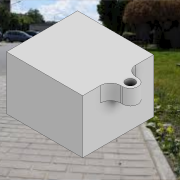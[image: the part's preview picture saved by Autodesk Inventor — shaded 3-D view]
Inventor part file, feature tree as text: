
AUTODESK INVENTOR PART (.ipt)
format: ipt  version: 2021 (Build 250183000, 183)  size: 265,216 bytes
history: native  units: mm
features: sketch x6, extrude x5, projected_geometry x3, hole x1, fillet x1
ambient origin geometry x8: Origin, YZ Plane, XZ Plane, XY Plane, X Axis, Y Axis, Z Axis, Center Point
bodies: Solid2 (feature_tree), Solid1 (feature_tree)
feature tree (16):
  extrude  "Extrusion1"  Depth=3.0mm TaperAngle=0.0deg
  extrude  "Extrusion2"  Depth=3.0mm TaperAngle=0.0deg
  extrude  "Extrusion3"  Depth=12.0mm
  extrude  "Extrusion4"  Depth=10.0mm
  extrude  "Extrusion5"  [1 undecoded]
  hole  "Hole1"  [1 undecoded]
  fillet  "Fillet1"  [1 undecoded]
  sketch  "Sketch1"  dims[d0=3.0mm d1=0.0mm d3=3.0mm d4=0.0mm]
  projected_geometry  "Projected Loop1"
  sketch  "Sketch2"  dims[d5=30.0mm d6=0.0mm d7=3.0mm d8=0.0mm]
  projected_geometry  "Projected Loop2"
  sketch  "Sketch3"  dims[d9=15.0mm d10=12.0mm]
  sketch  "Sketch4"  dims[d11=15.0mm d12=0.0mm]
  sketch  "Sketch5"  dims[d13=9.0mm d14=6.0mm d15=15.0mm d16=9.0mm d17=15.7mm d18=10.0mm d19=20.594885mm d20=10.0mm]
  projected_geometry  "Projected Loop3"
  sketch  "Sketch6"
note: 3 required parameter values undecoded (feature->parameter linkage not recoverable at this tier; creation-order binding heuristic only, values carry confidence <= 0.55)
